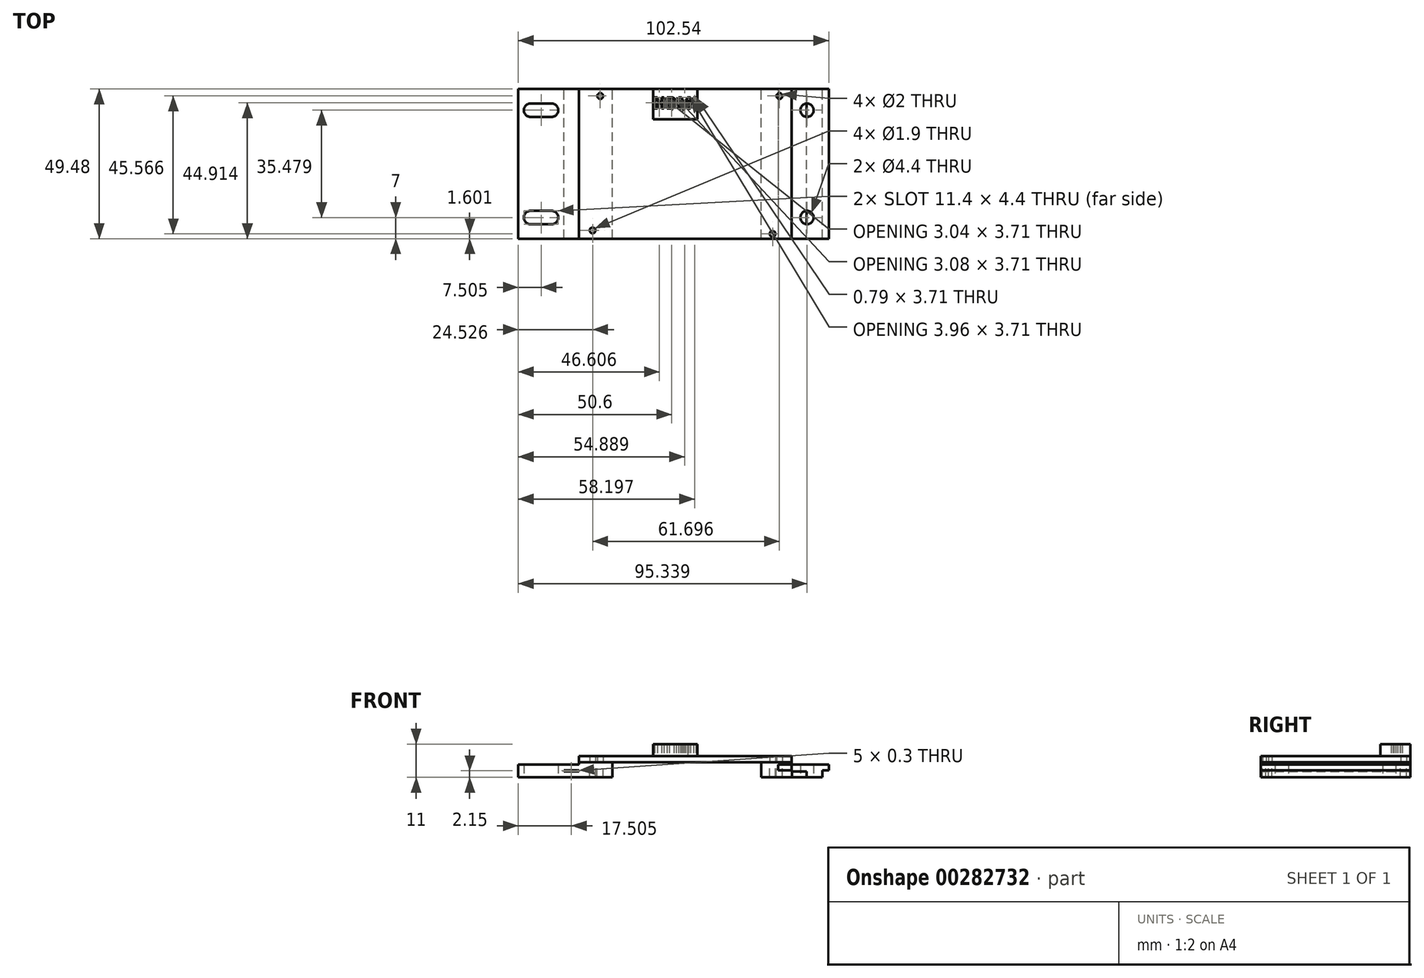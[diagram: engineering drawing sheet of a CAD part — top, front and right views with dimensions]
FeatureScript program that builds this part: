
annotation { "Feature Type Name" : "Feature", "Feature Type Description" : "" }
export const myFeature = defineFeature(function(context is Context, id is Id, definition is map)
    precondition{}
    {
        {
            var Q0;
            Q0=qCreatedBy(makeId("Top.planeOp"),FACE);
            var sketch = newSketch(context, id + "F0", { "sketchPlane" : qUnion([Q0])});
            skLineSegment(sketch, "E0.bottom", {"start": v(35.12, -24.74) * mm, "end": v(-35.12, -24.74) * mm});
            skLineSegment(sketch, "E0.top", {"start": v(35.12, 24.74) * mm, "end": v(-35.12, 24.74) * mm});
            skLineSegment(sketch, "E0.left", {"start": v(35.12, -24.74) * mm, "end": v(35.12, 24.74) * mm});
            skLineSegment(sketch, "E0.right", {"start": v(-35.12, -24.74) * mm, "end": v(-35.12, 24.74) * mm});
            skPoint(sketch, "E0.middle", {"position": v(0, 0) * mm});
            skPoint(sketch, "E1", {"position": v(-28.08, 22.43) * mm});
            skPoint(sketch, "E2", {"position": v(31.1, 22.43) * mm});
            skPoint(sketch, "E3", {"position": v(28.84, -23.14) * mm});
            skPoint(sketch, "E4", {"position": v(-30.6, -22) * mm});
            skCircle(sketch, "E5", {"center": v(-28.08, 22.43) * mm, "radius": 0.95 * mm});
            skCircle(sketch, "E6", {"center": v(31.1, 22.43) * mm, "radius": 0.95 * mm});
            skCircle(sketch, "E7", {"center": v(28.84, -23.14) * mm, "radius": 0.95 * mm});
            skCircle(sketch, "E8", {"center": v(-30.6, -22) * mm, "radius": 0.95 * mm});
            skSolve(sketch);
        }
        {
            var Q0;
            Q0 = qSketchRegion(id + "F0", true);
            extrude(context, id + "F1", {"entities" : qUnion([Q0]), "depth" : 2 * mm});
        }
        {
            var Q0;
            Q0=makeQuery(id+"F1.opExtrude","CAP_FACE",FACE,{"disambiguationData":[OSD([sQuery(id+"F0.wireOp",EDGE,"E0.bottom"),sQuery(id+"F0.wireOp",EDGE,"E0.top"),sQuery(id+"F0.wireOp",EDGE,"E0.left"),sQuery(id+"F0.wireOp",EDGE,"E0.right"),sQuery(id+"F0.wireOp",EDGE,"E5"),sQuery(id+"F0.wireOp",EDGE,"E6"),sQuery(id+"F0.wireOp",EDGE,"E7"),sQuery(id+"F0.wireOp",EDGE,"E8")])],"isStart":true});
            var sketch = newSketch(context, id + "F2", { "sketchPlane" : qUnion([Q0])});
            skLineSegment(sketch, "E9.bottom", {"start": v(-24.12, 24.74) * mm, "end": v(-35.12, 24.74) * mm});
            skLineSegment(sketch, "E9.top", {"start": v(-24.12, -24.74) * mm, "end": v(-35.12, -24.74) * mm});
            skLineSegment(sketch, "E9.left", {"start": v(-24.12, 24.74) * mm, "end": v(-24.12, -24.74) * mm});
            skLineSegment(sketch, "E9.right", {"start": v(-35.12, 24.74) * mm, "end": v(-35.12, -24.74) * mm});
            skLineSegment(sketch, "E10.bottom", {"start": v(25.12, 24.74) * mm, "end": v(35.12, 24.74) * mm});
            skLineSegment(sketch, "E10.top", {"start": v(25.12, -24.74) * mm, "end": v(35.12, -24.74) * mm});
            skLineSegment(sketch, "E10.left", {"start": v(25.12, 24.74) * mm, "end": v(25.12, -24.74) * mm});
            skLineSegment(sketch, "E10.right", {"start": v(35.12, 24.74) * mm, "end": v(35.12, -24.74) * mm});
            skSolve(sketch);
        }
        {
            var Q0;
            Q0 = qSketchRegion(id + "F2", true);
            extrude(context, id + "F3", {"entities" : qUnion([Q0]), "depth" : 3 * mm});
        }
        {
            var Q0;
            Q0=makeQuery(id+"F3.opExtrude","CAP_FACE",FACE,{"disambiguationData":[OSD([sQuery(id+"F2.wireOp",EDGE,"E9.bottom"),sQuery(id+"F2.wireOp",EDGE,"E9.top"),sQuery(id+"F2.wireOp",EDGE,"E9.left"),sQuery(id+"F2.wireOp",EDGE,"E9.right")])],"isStart":false});
            var sketch = newSketch(context, id + "F4", { "sketchPlane" : qUnion([Q0])});
            skLineSegment(sketch, "E11.bottom", {"start": v(-24.12, 24.74) * mm, "end": v(-40.12, 24.74) * mm});
            skLineSegment(sketch, "E11.top", {"start": v(-24.12, -24.74) * mm, "end": v(-40.12, -24.74) * mm});
            skLineSegment(sketch, "E11.left", {"start": v(-24.12, 24.74) * mm, "end": v(-24.12, -24.74) * mm});
            skLineSegment(sketch, "E11.right", {"start": v(-40.12, 24.74) * mm, "end": v(-40.12, -24.74) * mm});
            skSolve(sketch);
        }
        {
            var Q0;
            Q0 = qSketchRegion(id + "F4", true);
            extrude(context, id + "F5", {"entities" : qUnion([Q0]), "operationType" : NewBodyOperationType.ADD, "depth" : 2 * mm});
        }
        {
            var Q0;
            Q0=makeQuery(id+"F3.opExtrude","CAP_FACE",FACE,{"disambiguationData":[OSD([sQuery(id+"F2.wireOp",EDGE,"E10.bottom"),sQuery(id+"F2.wireOp",EDGE,"E10.top"),sQuery(id+"F2.wireOp",EDGE,"E10.left"),sQuery(id+"F2.wireOp",EDGE,"E10.right")])],"isStart":false});
            var sketch = newSketch(context, id + "F6", { "sketchPlane" : qUnion([Q0])});
            skLineSegment(sketch, "E12.bottom", {"start": v(25.12, 24.74) * mm, "end": v(40.12, 24.74) * mm});
            skLineSegment(sketch, "E12.top", {"start": v(25.12, -24.74) * mm, "end": v(40.12, -24.74) * mm});
            skLineSegment(sketch, "E12.left", {"start": v(25.12, 24.74) * mm, "end": v(25.12, -24.74) * mm});
            skLineSegment(sketch, "E12.right", {"start": v(40.12, 24.74) * mm, "end": v(40.12, -24.74) * mm});
            skSolve(sketch);
        }
        {
            var Q0;
            Q0 = qSketchRegion(id + "F6", true);
            extrude(context, id + "F7", {"entities" : qUnion([Q0]), "operationType" : NewBodyOperationType.ADD, "depth" : 2 * mm});
        }
        {
            var Q0;
            Q0=sQuery(id+"F0.wireOp",VERTEX,"E4");
            var Q1;
            Q1=sQuery(id+"F0.wireOp",VERTEX,"E1");
            var Q2;
            Q2=makeQuery(id+"F3.opExtrude","SWEPT_BODY",BODY,{"disambiguationData":[OSD([sQuery(id+"F2.wireOp",EDGE,"E9.bottom"),sQuery(id+"F2.wireOp",EDGE,"E9.top"),sQuery(id+"F2.wireOp",EDGE,"E9.left"),sQuery(id+"F2.wireOp",EDGE,"E9.right")])]});
            hole(context, id + "F8", {"style" : HoleStyle.SIMPLE, "endStyle" : HoleEndStyle.BLIND, "holeDiameter" : 2 * mm, "holeDepth" : 20 * mm, "tappedDepth" : 12 * mm, "tapClearance" : 3, "startFromSketch" : true, "locations" : qUnion([Q0, Q1]), "scope" : qUnion([Q2])});
        }
        {
            var Q0;
            Q0=sQuery(id+"F0.wireOp",VERTEX,"E2");
            var Q1;
            Q1=sQuery(id+"F0.wireOp",VERTEX,"E3");
            var Q2;
            Q2=makeQuery(id+"F3.opExtrude","SWEPT_BODY",BODY,{"disambiguationData":[OSD([sQuery(id+"F2.wireOp",EDGE,"E10.bottom"),sQuery(id+"F2.wireOp",EDGE,"E10.top"),sQuery(id+"F2.wireOp",EDGE,"E10.left"),sQuery(id+"F2.wireOp",EDGE,"E10.right")])]});
            hole(context, id + "F9", {"style" : HoleStyle.SIMPLE, "endStyle" : HoleEndStyle.BLIND, "holeDiameter" : 2 * mm, "holeDepth" : 20 * mm, "tappedDepth" : 12 * mm, "tapClearance" : 3, "startFromSketch" : true, "locations" : qUnion([Q0, Q1]), "scope" : qUnion([Q2])});
        }
        {
            var Q0;
            Q0=makeQuery(id+"F5.opExtrude","CAP_FACE",FACE,{"disambiguationData":[OSD([sQuery(id+"F4.wireOp",EDGE,"E11.bottom"),sQuery(id+"F4.wireOp",EDGE,"E11.top"),sQuery(id+"F4.wireOp",EDGE,"E11.left"),sQuery(id+"F4.wireOp",EDGE,"E11.right")])],"isStart":false});
            var sketch = newSketch(context, id + "F10", { "sketchPlane" : qUnion([Q0])});
            skLineSegment(sketch, "E13.bottom", {"start": v(-40.12, 24.74) * mm, "end": v(-55.12, 24.74) * mm});
            skLineSegment(sketch, "E13.top", {"start": v(-40.12, -24.74) * mm, "end": v(-55.12, -24.74) * mm});
            skLineSegment(sketch, "E13.left", {"start": v(-40.12, 24.74) * mm, "end": v(-40.12, -24.74) * mm});
            skLineSegment(sketch, "E13.right", {"start": v(-55.12, 24.74) * mm, "end": v(-55.12, -24.74) * mm});
            skLineSegment(sketch, "E14.bottom", {"start": v(47.42, 24.74) * mm, "end": v(57.42, 24.74) * mm});
            skLineSegment(sketch, "E14.top", {"start": v(47.42, -24.74) * mm, "end": v(57.42, -24.74) * mm});
            skLineSegment(sketch, "E14.left", {"start": v(47.42, 24.74) * mm, "end": v(47.42, -24.74) * mm});
            skLineSegment(sketch, "E14.right", {"start": v(57.42, 24.74) * mm, "end": v(57.42, -24.74) * mm});
            skLineSegment(sketch, "E15", {"start": v(-47.62, -24.74) * mm, "end": v(-47.62, 24.74) * mm, "construction": true});
            skLineSegment(sketch, "E16", {"start": v(52.42, -24.74) * mm, "end": v(52.42, 24.74) * mm, "construction": true});
            skLineSegment(sketch, "E17", {"start": v(-55.12, -17.74) * mm, "end": v(-40.12, -17.74) * mm, "construction": true});
            skLineSegment(sketch, "E18", {"start": v(-55.12, 17.74) * mm, "end": v(-40.12, 17.74) * mm, "construction": true});
            skLineSegment(sketch, "E19", {"start": v(47.42, -17.74) * mm, "end": v(57.42, -17.74) * mm, "construction": true});
            skLineSegment(sketch, "E20", {"start": v(47.42, 17.74) * mm, "end": v(57.42, 17.74) * mm, "construction": true});
            skPoint(sketch, "E21", {"position": v(-47.62, -17.74) * mm});
            skPoint(sketch, "E22", {"position": v(-47.62, 17.74) * mm});
            skPoint(sketch, "E23", {"position": v(52.42, -17.74) * mm});
            skPoint(sketch, "E24", {"position": v(52.42, 17.74) * mm});
            skPoint(sketch, "E25", {"position": v(-51.12, -17.74) * mm});
            skPoint(sketch, "E26", {"position": v(-44.12, -17.74) * mm});
            skPoint(sketch, "E27", {"position": v(-44.12, 17.74) * mm});
            skPoint(sketch, "E28", {"position": v(-51.12, 17.74) * mm});
            skArc(sketch, "E29", {"start": v(-51.12, -15.54) * mm, "mid": v(-53.32, -17.74) * mm, "end": v(-51.12, -19.94) * mm});
            skArc(sketch, "E30", {"start": v(-44.12, -19.94) * mm, "mid": v(-41.92, -17.74) * mm, "end": v(-44.12, -15.54) * mm});
            skLineSegment(sketch, "E31", {"start": v(-51.12, -19.94) * mm, "end": v(-44.12, -19.94) * mm});
            skLineSegment(sketch, "E32", {"start": v(-51.12, -15.54) * mm, "end": v(-44.12, -15.54) * mm});
            skLineSegment(sketch, "E33.MirrorCS", {"start": v(-51.12, 15.54) * mm, "end": v(-44.12, 15.54) * mm});
            skArc(sketch, "E34.MirrorCS", {"start": v(-44.12, 19.94) * mm, "mid": v(-41.92, 17.74) * mm, "end": v(-44.12, 15.54) * mm});
            skLineSegment(sketch, "E35.MirrorCS", {"start": v(-51.12, 19.94) * mm, "end": v(-44.12, 19.94) * mm});
            skArc(sketch, "E36.MirrorCS", {"start": v(-51.12, 15.54) * mm, "mid": v(-53.32, 17.74) * mm, "end": v(-51.12, 19.94) * mm});
            skSolve(sketch);
        }
        {
            var Q0;
            Q0 = qSketchRegion(id + "F10", true);
            extrude(context, id + "F11", {"entities" : qUnion([Q0]), "oppositeDirection" : true, "depth" : 2.3 * mm});
        }
        {
            var Q0;
            Q0=makeQuery(id+"F11.opExtrude","CAP_FACE",FACE,{"disambiguationData":[OSD([sQuery(id+"F10.wireOp",EDGE,"E13.bottom"),sQuery(id+"F10.wireOp",EDGE,"E13.top"),sQuery(id+"F10.wireOp",EDGE,"E13.left"),sQuery(id+"F10.wireOp",EDGE,"E13.right")])],"isStart":false});
            var sketch = newSketch(context, id + "F12", { "sketchPlane" : qUnion([Q0])});
            skLineSegment(sketch, "E37.bottom", {"start": v(-55.12, 24.74) * mm, "end": v(-35.12, 24.74) * mm});
            skLineSegment(sketch, "E37.top", {"start": v(-55.12, -24.74) * mm, "end": v(-35.12, -24.74) * mm});
            skLineSegment(sketch, "E37.left", {"start": v(-55.12, 24.74) * mm, "end": v(-55.12, -24.74) * mm});
            skLineSegment(sketch, "E37.right", {"start": v(-35.12, 24.74) * mm, "end": v(-35.12, -24.74) * mm});
            skLineSegment(sketch, "E38", {"start": v(-55.12, 24.74) * mm, "end": v(-55.12, 24.74) * mm});
            skSolve(sketch);
        }
        {
            var Q0;
            Q0 = qSketchRegion(id + "F12", true);
            extrude(context, id + "F13", {"entities" : qUnion([Q0]), "operationType" : NewBodyOperationType.ADD, "depth" : 2 * mm});
        }
        {
            var Q0;
            Q0=makeQuery(id+"F11.opExtrude","CAP_FACE",FACE,{"disambiguationData":[OSD([sQuery(id+"F10.wireOp",EDGE,"E14.bottom"),sQuery(id+"F10.wireOp",EDGE,"E14.top"),sQuery(id+"F10.wireOp",EDGE,"E14.left"),sQuery(id+"F10.wireOp",EDGE,"E14.right")])],"isStart":false});
            var sketch = newSketch(context, id + "F14", { "sketchPlane" : qUnion([Q0])});
            skLineSegment(sketch, "E39.bottom", {"start": v(61.92, 24.74) * mm, "end": v(42.92, 24.74) * mm});
            skLineSegment(sketch, "E39.top", {"start": v(61.92, -24.74) * mm, "end": v(42.92, -24.74) * mm});
            skLineSegment(sketch, "E39.left", {"start": v(61.92, 24.74) * mm, "end": v(61.92, -24.74) * mm});
            skLineSegment(sketch, "E39.right", {"start": v(42.92, 24.74) * mm, "end": v(42.92, -24.74) * mm});
            skSolve(sketch);
        }
        {
            var Q0;
            Q0 = qSketchRegion(id + "F14", true);
            extrude(context, id + "F15", {"entities" : qUnion([Q0]), "operationType" : NewBodyOperationType.ADD, "depth" : 2 * mm});
        }
        {
            var Q0;
            Q0=makeQuery(id+"F1.opExtrude","CAP_FACE",FACE,{"disambiguationData":[OSD([sQuery(id+"F0.wireOp",EDGE,"E0.bottom"),sQuery(id+"F0.wireOp",EDGE,"E0.top"),sQuery(id+"F0.wireOp",EDGE,"E0.left"),sQuery(id+"F0.wireOp",EDGE,"E0.right"),sQuery(id+"F0.wireOp",EDGE,"E5"),sQuery(id+"F0.wireOp",EDGE,"E6"),sQuery(id+"F0.wireOp",EDGE,"E7"),sQuery(id+"F0.wireOp",EDGE,"E8")])],"isStart":false});
            var sketch = newSketch(context, id + "F16", { "sketchPlane" : qUnion([Q0])});
            skLineSegment(sketch, "E40.bottom", {"start": v(-10.63, 24.74) * mm, "end": v(4.03, 24.74) * mm});
            skLineSegment(sketch, "E40.top", {"start": v(-10.63, 14.74) * mm, "end": v(4.03, 14.74) * mm});
            skLineSegment(sketch, "E40.left", {"start": v(-10.63, 24.74) * mm, "end": v(-10.63, 14.74) * mm});
            skLineSegment(sketch, "E40.right", {"start": v(4.03, 24.74) * mm, "end": v(4.03, 14.74) * mm});
            skText(sketch, "E41", { "text": "HDMI", "fontName": "OpenSans-Bold.ttf"});
            skPoint(sketch, "E42", {"position": v(4.03, 19.74) * mm});
            const initialGuessF16  = {"E41": [-0.0105, 0.01832, 1, 0, 0.00374]};
            skSetInitialGuess(sketch, initialGuessF16);
            skSolve(sketch);
        }
        {
            var Q0;
            Q0=sQuery(id+"F10.wireOp",VERTEX,"E21");
            var Q1;
            Q1=sQuery(id+"F10.wireOp",VERTEX,"E22");
            var Q2;
            Q2=sQuery(id+"F10.wireOp",VERTEX,"E23");
            var Q3;
            Q3=sQuery(id+"F10.wireOp",VERTEX,"E24");
            var Q4;
            Q4=makeQuery(id+"F11.opExtrude","SWEPT_BODY",BODY,{"disambiguationData":[OSD([sQuery(id+"F10.wireOp",EDGE,"E13.bottom"),sQuery(id+"F10.wireOp",EDGE,"E13.top"),sQuery(id+"F10.wireOp",EDGE,"E13.left"),sQuery(id+"F10.wireOp",EDGE,"E13.right")])]});
            var Q5;
            Q5=makeQuery(id+"F11.opExtrude","SWEPT_BODY",BODY,{"disambiguationData":[OSD([sQuery(id+"F10.wireOp",EDGE,"E14.bottom"),sQuery(id+"F10.wireOp",EDGE,"E14.top"),sQuery(id+"F10.wireOp",EDGE,"E14.left"),sQuery(id+"F10.wireOp",EDGE,"E14.right")])]});
            hole(context, id + "F17", {"style" : HoleStyle.SIMPLE, "endStyle" : HoleEndStyle.BLIND, "standardTappedOrClearance" : lookupTablePath({ "standard" : "ISO", "fit" : "Normal", "size" : "M4", "type" : "Clearance" }), "standardBlindInLast" : lookupTablePath({ "fit" : "Standard", "standard" : "ISO", "size" : "M4", "type" : "Clearance" }), "holeDiameter" : 4.4 * mm, "holeDepth" : 20 * mm, "tappedDepth" : 12 * mm, "tapClearance" : 3, "locations" : qUnion([Q0, Q1, Q2, Q3]), "scope" : qUnion([Q4, Q5])});
        }
        {
            var Q0;
            Q0 = qSketchRegion(id + "F16", true);
            var Q1;
            Q1=makeQuery(id+"F16.imprint","IMPRINT",FACE,{"disambiguationData":[TD([[makeQuery(id+"F16.imprint","IMPRINT",EDGE,{"derivedFrom":sQuery(id+"F16.wireOp",EDGE,"E41.sketch_text.stroke-19")}),1.0]])]});
            extrude(context, id + "F18", {"entities" : qUnion([Q0, Q1]), "depth" : 4 * mm});
        }
        {
            var Q0;
            Q0=makeQuery(id+"F11.opExtrude","SWEPT_BODY",BODY,{"disambiguationData":[OSD([sQuery(id+"F10.wireOp",EDGE,"E14.bottom"),sQuery(id+"F10.wireOp",EDGE,"E14.top"),sQuery(id+"F10.wireOp",EDGE,"E14.left"),sQuery(id+"F10.wireOp",EDGE,"E14.right")])]});
            transform(context, id + "F19", {"entities" : qUnion([Q0]), "transformType" : TransformType.TRANSLATION_3D, "dx" : -12.2 * mm, "dy" : 0 * mm, "dz" : 0 * mm, "makeCopy" : false});
        }
        {
            var Q0;
            Q0=makeQuery(id+"F10.imprint","IMPRINT",FACE,{"disambiguationData":[TD([[makeQuery(id+"F10.imprint","IMPRINT",EDGE,{"derivedFrom":sQuery(id+"F10.wireOp",EDGE,"E14.bottom")}),-1.0]])]});
            var Q1;
            Q1=makeQuery(id+"F10.imprint","IMPRINT",FACE,{"disambiguationData":[TD([[makeQuery(id+"F10.imprint","IMPRINT",EDGE,{"derivedFrom":sQuery(id+"F10.wireOp",EDGE,"E29")}),1.0]])]});
            var Q2;
            Q2=makeQuery(id+"F10.imprint","IMPRINT",FACE,{"disambiguationData":[TD([[makeQuery(id+"F10.imprint","IMPRINT",EDGE,{"derivedFrom":sQuery(id+"F10.wireOp",EDGE,"E33.MirrorCS")}),1.0]])]});
            extrude(context, id + "F20", {"entities" : qUnion([Q0, Q1, Q2]), "operationType" : NewBodyOperationType.REMOVE, "oppositeDirection" : true, "depth" : 25 * mm});
        }
    });
